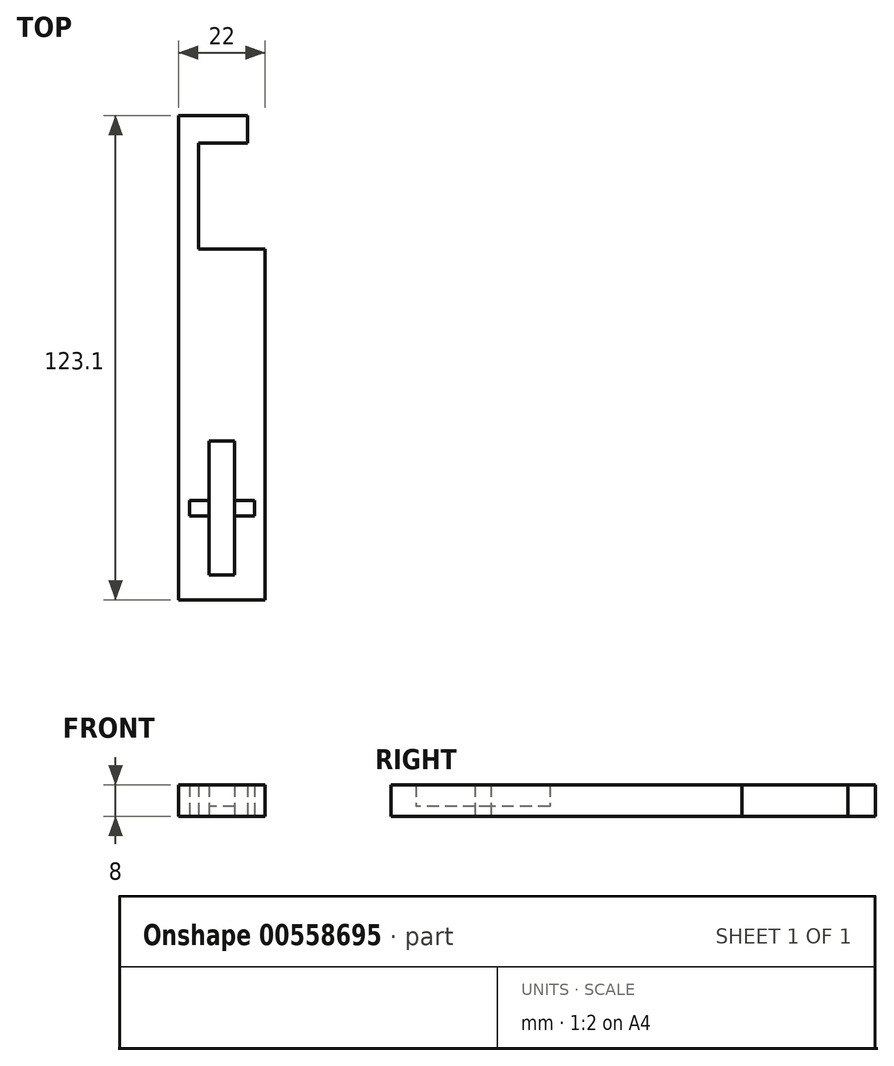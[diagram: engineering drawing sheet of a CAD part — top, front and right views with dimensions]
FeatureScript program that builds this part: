
annotation { "Feature Type Name" : "Feature", "Feature Type Description" : "" }
export const myFeature = defineFeature(function(context is Context, id is Id, definition is map)
    precondition{}
    {
        {
            var Q0;
            Q0=qCreatedBy(makeId("Top.planeOp"),FACE);
            var sketch = newSketch(context, id + "F0", { "sketchPlane" : qUnion([Q0])});
            skLineSegment(sketch, "E0.bottom", {"start": v(11, 44.55) * mm, "end": v(-11, 44.55) * mm});
            skLineSegment(sketch, "E0.top", {"start": v(11, -44.55) * mm, "end": v(-11, -44.55) * mm});
            skLineSegment(sketch, "E0.left", {"start": v(11, 44.55) * mm, "end": v(11, -44.55) * mm});
            skLineSegment(sketch, "E0.right", {"start": v(-11, 44.55) * mm, "end": v(-11, -44.55) * mm});
            skPoint(sketch, "E0.middle", {"position": v(0, 0) * mm});
            skLineSegment(sketch, "E1.bottom", {"start": v(3.25, -4.22) * mm, "end": v(-3.25, -4.22) * mm});
            skLineSegment(sketch, "E1.top", {"start": v(3.25, -38.22) * mm, "end": v(-3.25, -38.22) * mm});
            skLineSegment(sketch, "E1.left", {"start": v(3.25, -4.22) * mm, "end": v(3.25, -38.22) * mm});
            skLineSegment(sketch, "E1.right", {"start": v(-3.25, -4.22) * mm, "end": v(-3.25, -38.22) * mm});
            skPoint(sketch, "E1.middle", {"position": v(0, -21.22) * mm});
            skLineSegment(sketch, "E2.bottom", {"start": v(-11, 44.55) * mm, "end": v(-6, 44.55) * mm});
            skLineSegment(sketch, "E3.bottom", {"start": v(11, 44.55) * mm, "end": v(1.5, 44.55) * mm});
            skLineSegment(sketch, "E4.bottom", {"start": v(-11, 44.55) * mm, "end": v(-5.94, 44.55) * mm});
            skLineSegment(sketch, "E4.top", {"start": v(-11, 78.55) * mm, "end": v(-5.94, 78.55) * mm});
            skLineSegment(sketch, "E4.left", {"start": v(-11, 44.55) * mm, "end": v(-11, 78.55) * mm});
            skLineSegment(sketch, "E4.right", {"start": v(-5.94, 44.55) * mm, "end": v(-5.94, 78.55) * mm});
            skLineSegment(sketch, "E5.bottom", {"start": v(-5.94, 78.55) * mm, "end": v(6.56, 78.55) * mm});
            skLineSegment(sketch, "E5.top", {"start": v(-5.94, 71.55) * mm, "end": v(6.56, 71.55) * mm});
            skLineSegment(sketch, "E5.left", {"start": v(-5.94, 78.55) * mm, "end": v(-5.94, 71.55) * mm});
            skLineSegment(sketch, "E5.right", {"start": v(6.56, 78.55) * mm, "end": v(6.56, 71.55) * mm});
            skLineSegment(sketch, "E6.bottom", {"start": v(8.25, -23.22) * mm, "end": v(-8.25, -23.22) * mm});
            skLineSegment(sketch, "E6.top", {"start": v(8.25, -19.22) * mm, "end": v(-8.25, -19.22) * mm});
            skLineSegment(sketch, "E6.left", {"start": v(8.25, -23.22) * mm, "end": v(8.25, -19.22) * mm});
            skLineSegment(sketch, "E6.right", {"start": v(-8.25, -23.22) * mm, "end": v(-8.25, -19.22) * mm});
            skSolve(sketch);
        }
        {
            var Q0;
            Q0=makeQuery(id+"F0.imprint","IMPRINT",FACE,{"disambiguationData":[TD([[makeQuery(id+"F0.imprint","IMPRINT",EDGE,{"derivedFrom":sQuery(id+"F0.wireOp",EDGE,"Pqc5xqcg-Qgv8-XXyU-ekZD-nZ5gzvdi3LpR.bottom")}),-1.0]])]});
            var Q1;
            Q1=makeQuery(id+"F0.imprint","IMPRINT",FACE,{"disambiguationData":[TD([[makeQuery(id+"F0.imprint","IMPRINT",EDGE,{"derivedFrom":sQuery(id+"F0.wireOp",EDGE,"E2.bottom")}),1.0]])]});
            var Q2;
            Q2=makeQuery(id+"F0.imprint","IMPRINT",FACE,{"disambiguationData":[TD([[makeQuery(id+"F0.imprint","IMPRINT",EDGE,{"derivedFrom":sQuery(id+"F0.wireOp",EDGE,"E0.bottom")}),1.0]])]});
            var Q3;
            Q3=makeQuery(id+"F0.imprint","IMPRINT",FACE,{"disambiguationData":[TD([[makeQuery(id+"F0.imprint","IMPRINT",EDGE,{"derivedFrom":sQuery(id+"F0.wireOp",EDGE,"E3.bottom")}),-1.0]])]});
            var Q4;
            Q4=makeQuery(id+"F0.imprint","IMPRINT",FACE,{"disambiguationData":[TD([[makeQuery(id+"F0.imprint","IMPRINT",EDGE,{"derivedFrom":sQuery(id+"F0.wireOp",EDGE,"HnQft3v9-mSai-PtbU-x4zt-C10cOCln6Zu0.bottom")}),1.0]])]});
            var Q5;
            Q5=makeQuery(id+"F0.imprint","IMPRINT",FACE,{"disambiguationData":[TD([[makeQuery(id+"F0.imprint","IMPRINT",EDGE,{"derivedFrom":sQuery(id+"F0.wireOp",EDGE,"E4.top")}),-1.0]])]});
            var Q6;
            Q6=makeQuery(id+"F0.imprint","IMPRINT",FACE,{"disambiguationData":[TD([[makeQuery(id+"F0.imprint","IMPRINT",EDGE,{"derivedFrom":sQuery(id+"F0.wireOp",EDGE,"E5.bottom")}),-1.0]])]});
            extrude(context, id + "F1", {"entities" : qUnion([Q0, Q1, Q2, Q3, Q4, Q5, Q6]), "depth" : 8 * mm, "offsetDistance" : 25 * mm});
        }
        {
            var Q0;
            {var subQ0=sQuery(id+"F0.wireOp",EDGE,"E1.top");Q0=makeQuery(id+"F0.imprint","IMPRINT",FACE,{"disambiguationData":[TD([[makeQuery(id+"F0.imprint","IMPRINT",EDGE,{"derivedFrom":subQ0}),-1.0]])]});}
            var Q1;
            {var subQ0=sQuery(id+"F0.wireOp",EDGE,"u58vRcST-Of1m-cP55-t3Zi-zrGPtjlhGXBe");var subQ1=sQuery(id+"F0.wireOp",EDGE,"E1.left");var subQ2=makeQuery(id+"F0.imprint","INTERSECT",VERTEX,{"disambiguationData":[OD(0.0)],"derivedFrom":[subQ1,subQ0]});Q1=makeQuery(id+"F0.imprint","IMPRINT",FACE,{"disambiguationData":[TD([[makeQuery(id+"F0.imprint","IMPRINT",EDGE,{"disambiguationData":[TD([[subQ2,-1.0]])],"derivedFrom":subQ1}),-1.0]])]});}
            var Q2;
            {var subQ0=sQuery(id+"F0.wireOp",EDGE,"E1.bottom");Q2=makeQuery(id+"F0.imprint","IMPRINT",FACE,{"disambiguationData":[TD([[makeQuery(id+"F0.imprint","IMPRINT",EDGE,{"derivedFrom":subQ0}),1.0]])]});}
            var Q3;
            {var subQ0=sQuery(id+"F0.wireOp",EDGE,"u58vRcST-Of1m-cP55-t3Zi-zrGPtjlhGXBe");var subQ1=sQuery(id+"F0.wireOp",EDGE,"E1.left");var subQ2=makeQuery(id+"F0.imprint","INTERSECT",VERTEX,{"disambiguationData":[OD(0.0)],"derivedFrom":[subQ1,subQ0]});Q3=makeQuery(id+"F0.imprint","IMPRINT",FACE,{"disambiguationData":[TD([[makeQuery(id+"F0.imprint","IMPRINT",EDGE,{"disambiguationData":[TD([[subQ2,-1.0]])],"derivedFrom":subQ1}),1.0]])]});}
            var Q4;
            {var subQ0=sQuery(id+"F0.wireOp",EDGE,"u58vRcST-Of1m-cP55-t3Zi-zrGPtjlhGXBe");var subQ1=sQuery(id+"F0.wireOp",EDGE,"E1.right");var subQ2=makeQuery(id+"F0.imprint","INTERSECT",VERTEX,{"disambiguationData":[OD(0.0)],"derivedFrom":[subQ1,subQ0]});Q4=makeQuery(id+"F0.imprint","IMPRINT",FACE,{"disambiguationData":[TD([[makeQuery(id+"F0.imprint","IMPRINT",EDGE,{"disambiguationData":[TD([[subQ2,-1.0]])],"derivedFrom":subQ1}),-1.0]])]});}
            extrude(context, id + "F2", {"entities" : qUnion([Q0, Q1, Q2, Q3, Q4]), "operationType" : NewBodyOperationType.ADD, "depth" : 2.5 * mm, "offsetDistance" : 25 * mm});
        }
    });
